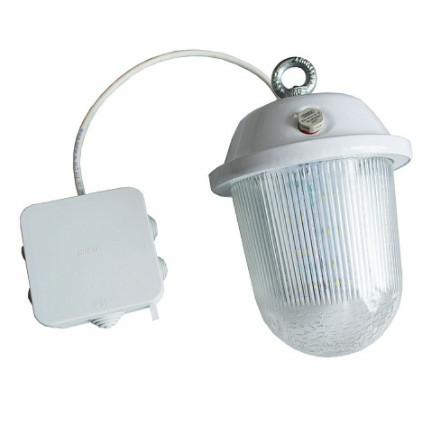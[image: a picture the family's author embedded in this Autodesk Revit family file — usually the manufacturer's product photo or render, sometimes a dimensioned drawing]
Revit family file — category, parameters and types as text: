
# Revit family: GALAD Желудь LED
name_source: partatom
category: Осветительные приборы
revit_build: Autodesk Revit 2018 (Build: 20180423_1000(x64)
units: mm (PartAtom-declared; Revit-internal decimal feet)

## family parameters
Источник света = Да
Общий = Нет
Основа = Грань
При загрузке вырезать с полостями = Нет
Размер круглого соединителя = Использовать диаметр
Тип детали = Нормальный
Точка расчета площади = Нет

## types (2) — shared parameters
ADSK_Версия Revit = 2018
ADSK_Версия семейства = 1.01
ADSK_Единица измерения = шт.
ADSK_Завод-изготовитель = АО «КАДОШКИНСКИЙ ЭЛЕКТРОТЕХНИЧЕСКИЙ ЗАВОД»
ADSK_Классификация нагрузок = Освещение
ADSK_Количество = 1
ADSK_Количество фаз = 1
ADSK_Коэффициент мощности = 0.95
ADSK_Масса = 1.51
ADSK_Масса_Текст = 1.51
ADSK_Напряжение = 36 В
ADSK_Номинальная мощность = 12 В·А
ADSK_Обозначение = ГОСТ 15150-69
ADSK_Полная мощность = 13 В·А
ADSK_Размер_Высота = 236 мм
ADSK_Размер_Длина = 156 мм
ADSK_Размер_Ширина = 156 мм
ADSK_Ток = 0 А
ADSK_Энергоэффективность = 100 лм/Вт
IP = 65
URL = https://galad.ru
Блок аварийного питания = Нет
Возможный угол наклона = 0
Группа модели = Светильники
Изготовитель = АО «КАДОШКИНСКИЙ ЭЛЕКТРОТЕХНИЧЕСКИЙ ЗАВОД»
Класс Защиты = 1
Класс защиты от поражения электрическим током = 3
Класс светораспределения = П
Климатическая зона = У2
Климатическое исполнение = -45…40 °С
Коэффициент пульсации = менее 5%
Материал корпуса = Сталь
Материал рассеивателя = Стекло жёлудя
Область использования = ЖКХ
Описание = Светильник серии GALAD Желудь LED предназначен для освещения промышленных предприятий, строительных и складских объектов, автостоянок и парковок.
Отметка по умолчанию = 1219 мм
Полная установленная мощность = 13 В·А
Световая отдача = 100
Светофильтр = 16777215
Смещение цветовой температуры при затухании лампы = <Нет>
Снижение светового потока во время разгорания = не более 6%
Срок службы = 12 лет
Тип КСС = специальная
Тип ПРА = ЭПРА
Тип источника света = LED
Тип монтажной поверхности = Подвес
Тип продукции = Светильник
Тип устройства управления светодиодами = без управления
Угол наклона = -90.00°
Частота = 50
zero-valued in all types: Неравномерность яркости, Цветопередача

## per-type parameters (varying)
| type | ADSK_Код изделия | Диапазон цветовой температуры | Файл фотометрической сетки |
| GALAD Желудь LED-12/Р/5000 | 17119 | 5028±283 | GALAD zhelud LED-12P5000.ies |
| GALAD Желудь LED-12/Р/3000 | 17120 | 3045±175 | GALAD zhelud LED-12P3000.ies |

note: column(s) folded — value = type name in every type: ADSK_Марка, ADSK_Наименование, ADSK_Наименование краткое
